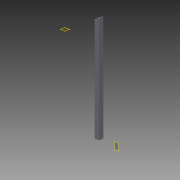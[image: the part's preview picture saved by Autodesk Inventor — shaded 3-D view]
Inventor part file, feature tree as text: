
AUTODESK INVENTOR PART (.ipt)
format: ipt  version: 2013 (Build 170138000, 138)  size: 101,888 bytes
history: native  units: in
note: dims shown in document units (in); Inventor stores cm internally (conversion verified against a paired STEP export)
features: extrude x4, sketch x4, plane x2
ambient origin geometry x8: Origin, YZ Plane, XZ Plane, XY Plane, X Axis, Y Axis, Z Axis, Center Point
bodies: Solid1 (feature_tree)
feature tree (10):
  extrude  "Extrusion1"  Depth=1.0in
  plane  "Work Plane1"
  extrude  "Extrusion3"  Depth=40.0in TaperAngle=0.0deg
  plane  "Work Plane2"
  extrude  "Extrusion4"  Depth=100.0in TaperAngle=0.0deg
  extrude  "Extrusion5"  Depth=1.0in TaperAngle=0.0deg
  sketch  "Sketch1"  dims[d0=1.0in d2=1.0in]
  sketch  "Sketch4"  dims[d3=0.0625in d4=40.0in d5=0.0in]
  sketch  "Sketch5"  dims[d8=100.0in d9=0.0in d10=100.0in d11=0.0in]
  sketch  "Sketch6"  dims[d12=0.5in d14=1.0in d15=0.0in]
